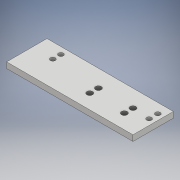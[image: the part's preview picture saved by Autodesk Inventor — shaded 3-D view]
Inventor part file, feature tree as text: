
AUTODESK INVENTOR PART (.ipt)
format: ipt  version: 2018 (Build 220112000, 112)  size: 136,704 bytes
history: native  units: mm
features: thread x4, sketch x3, hole x2, extrude x1
ambient origin geometry x8: Origin, YZ Plane, XZ Plane, XY Plane, X Axis, Y Axis, Z Axis, Center Point
bodies: Solid1 (feature_tree)
feature tree (10):
  extrude  "Extrusion1"  Depth=10.0mm
  hole  "Hole1"  [1 undecoded]
  hole  "Hole2"  [1 undecoded]
  thread  "Thread1"  [1 undecoded]
  thread  "Thread2"  [1 undecoded]
  thread  "Thread3"  [1 undecoded]
  thread  "Thread4"  [1 undecoded]
  sketch  "Sketch1"  dims[d2=10.0mm d3=0.0mm d32=32.0mm]
  sketch  "Sketch7"  dims[d34=10.0mm d36=17.0mm]
  sketch  "Sketch8"  dims[d37=10.0mm d41=36.0mm d42=12.0mm d43=14.0mm d44=8.5mm d45=6.0mm d46=4.0mm d47=2.0mm d48=90.0deg d49=0.5mm d50=20.594885mm d58=30.0mm d59=15.0mm d60=40.0mm d61=60.0mm d62=15.0mm d63=10.0mm d64=6.0mm d65=4.0mm d66=2.0mm d67=90.0deg d68=0.5mm d69=20.594885mm d70=15.0mm d71=10.0mm d72=0.0mm d73=10.0mm d74=0.0mm d75=10.0mm d76=0.0mm d77=10.0mm d78=0.0mm d81=219.0mm d82=70.0mm d83=90.0deg d84=219.0mm]
note: 6 required parameter values undecoded (feature->parameter linkage not recoverable at this tier; creation-order binding heuristic only, values carry confidence <= 0.55)
